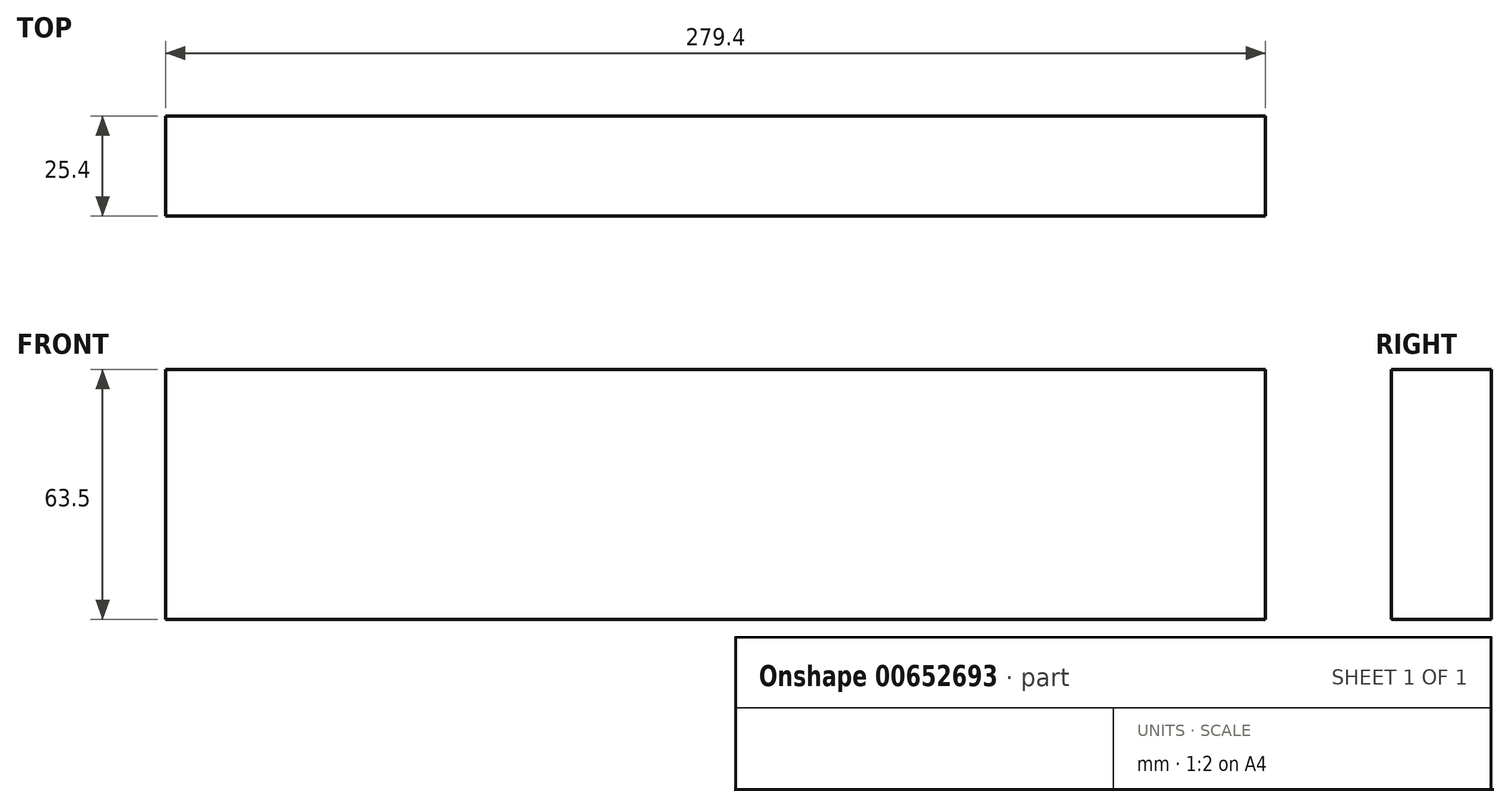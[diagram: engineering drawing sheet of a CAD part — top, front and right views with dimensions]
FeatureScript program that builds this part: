
annotation { "Feature Type Name" : "Feature", "Feature Type Description" : "" }
export const myFeature = defineFeature(function(context is Context, id is Id, definition is map)
    precondition{}
    {
        {
            var Q0;
            Q0=qCreatedBy(makeId("Front.planeOp"),FACE);
            var sketch = newSketch(context, id + "F0", { "sketchPlane" : qUnion([Q0])});
            skLineSegment(sketch, "E0.bottom", {"start": v(-139.7, -31.75) * mm, "end": v(139.7, -31.75) * mm});
            skLineSegment(sketch, "E0.top", {"start": v(-139.7, 31.75) * mm, "end": v(139.7, 31.75) * mm});
            skLineSegment(sketch, "E0.left", {"start": v(-139.7, -31.75) * mm, "end": v(-139.7, 31.75) * mm});
            skLineSegment(sketch, "E0.right", {"start": v(139.7, -31.75) * mm, "end": v(139.7, 31.75) * mm});
            skPoint(sketch, "E0.middle", {"position": v(0, 0) * mm});
            skSolve(sketch);
        }
        {
            var Q0;
            Q0=makeQuery(id+"F0.imprint","IMPRINT",FACE,{"disambiguationData":[TD([[makeQuery(id+"F0.imprint","IMPRINT",EDGE,{"derivedFrom":sQuery(id+"F0.wireOp",EDGE,"E0.bottom")}),1.0]])]});
            var sketch = newSketch(context, id + "F1", { "sketchPlane" : qUnion([Q0])});
            skCircle(sketch, "E1", {"center": v(0, 0) * mm, "radius": 20.83 * mm});
            skSolve(sketch);
        }
        {
            var Q0;
            Q0=makeQuery(id+"F0.imprint","IMPRINT",FACE,{"disambiguationData":[TD([[makeQuery(id+"F0.imprint","IMPRINT",EDGE,{"derivedFrom":sQuery(id+"F0.wireOp",EDGE,"E0.bottom")}),1.0]])]});
            extrude(context, id + "F2", {"entities" : qUnion([Q0]), "depth" : 25.4 * mm, "offsetDistance" : 25.4 * mm});
        }
        {
            var Q0;
            Q0=sQuery(id+"F1.wireOp",EDGE,"E1");
            extrude(context, id + "F3", {"bodyType" : ToolBodyType.SURFACE, "surfaceEntities" : qUnion([Q0]), "endBound" : BoundingType.THROUGH_ALL, "oppositeDirection" : true, "depth" : 25.4 * mm, "offsetDistance" : 25.4 * mm});
        }
    });
